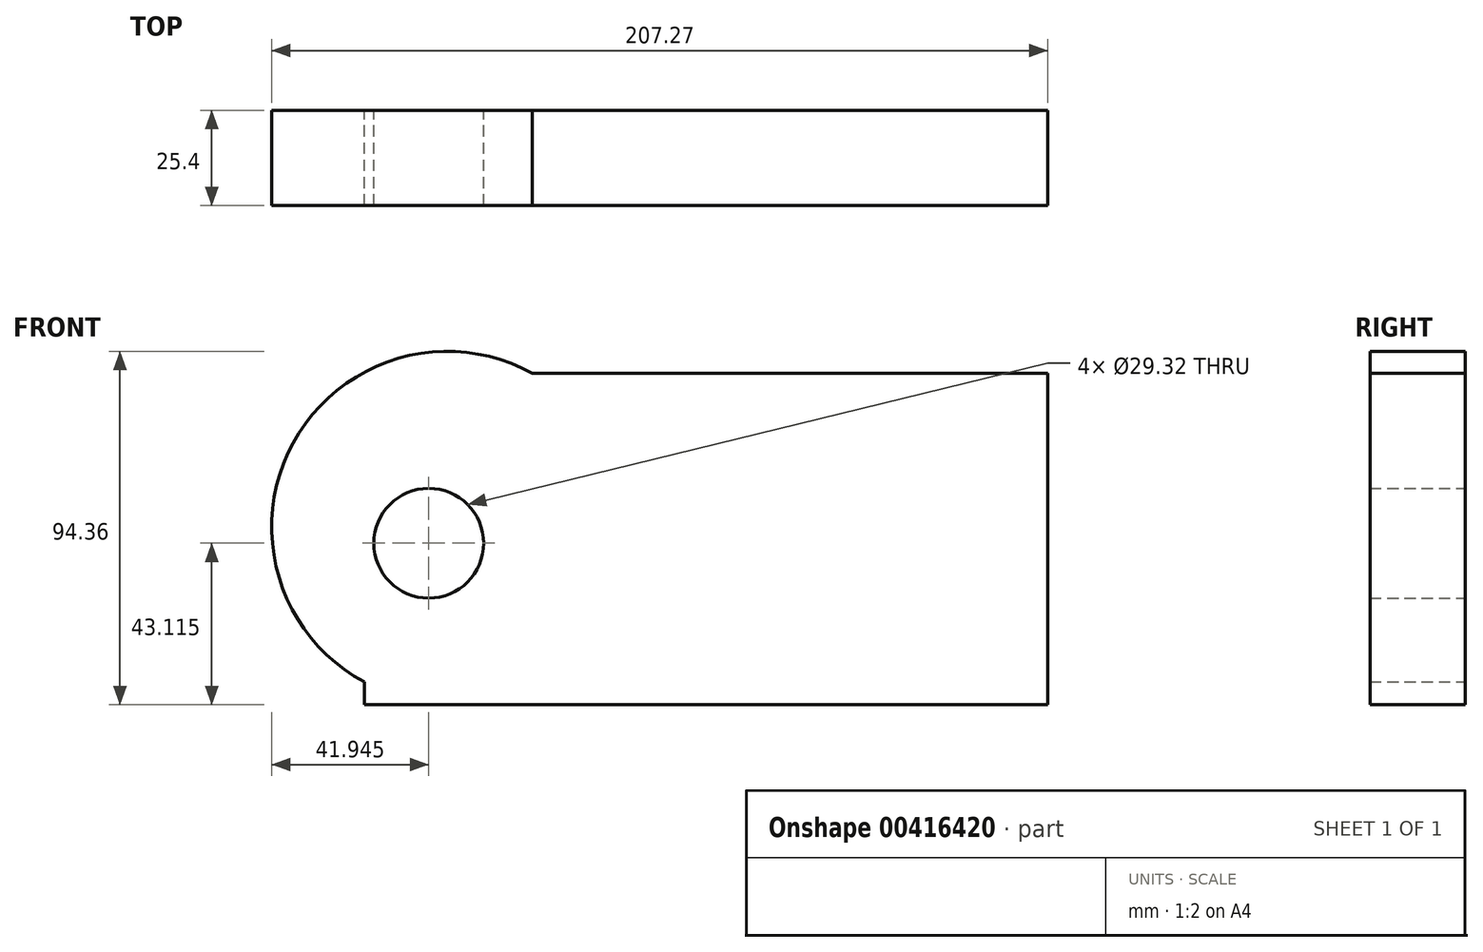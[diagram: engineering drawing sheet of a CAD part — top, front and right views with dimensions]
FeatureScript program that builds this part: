
annotation { "Feature Type Name" : "Feature", "Feature Type Description" : "" }
export const myFeature = defineFeature(function(context is Context, id is Id, definition is map)
    precondition{}
    {
        {
            var Q0;
            Q0=qCreatedBy(makeId("Front.planeOp"),FACE);
            var sketch = newSketch(context, id + "F0", { "sketchPlane" : qUnion([Q0])});
            skLineSegment(sketch, "E0.bottom", {"start": v(-123, 51.29) * mm, "end": v(59.55, 51.29) * mm});
            skLineSegment(sketch, "E0.top", {"start": v(-123, -37.22) * mm, "end": v(59.55, -37.22) * mm});
            skLineSegment(sketch, "E0.left", {"start": v(-123, 51.29) * mm, "end": v(-123, -37.22) * mm});
            skLineSegment(sketch, "E0.right", {"start": v(59.55, 51.29) * mm, "end": v(59.55, -37.22) * mm});
            skCircle(sketch, "E1", {"center": v(-105.77, 5.9) * mm, "radius": 14.66 * mm});
            skCircle(sketch, "E2", {"center": v(-100.78, 10.2) * mm, "radius": 46.94 * mm});
            skSolve(sketch);
        }
        {
            var Q0;
            Q0 = qSketchRegion(id + "F0", true);
            extrude(context, id + "F1", {"entities" : qUnion([Q0]), "depth" : 25.4 * mm});
        }
    });
